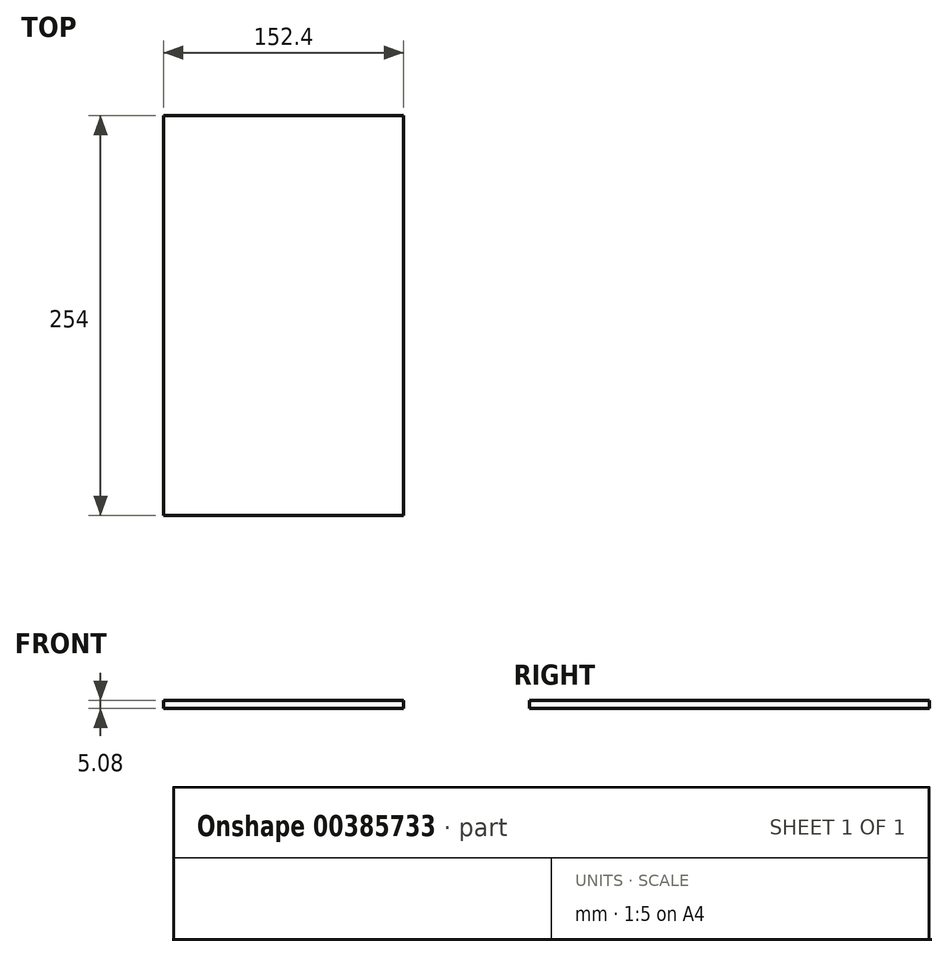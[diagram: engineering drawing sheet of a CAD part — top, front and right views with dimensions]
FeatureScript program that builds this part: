
annotation { "Feature Type Name" : "Feature", "Feature Type Description" : "" }
export const myFeature = defineFeature(function(context is Context, id is Id, definition is map)
    precondition{}
    {
        {
            var Q0;
            Q0=qCreatedBy(makeId("Front.planeOp"),FACE);
            var sketch = newSketch(context, id + "F0", { "sketchPlane" : qUnion([Q0])});
            skLineSegment(sketch, "E0.bottom", {"start": v(-76.2, 2.54) * mm, "end": v(76.2, 2.54) * mm});
            skLineSegment(sketch, "E0.top", {"start": v(-76.2, -2.54) * mm, "end": v(76.2, -2.54) * mm});
            skLineSegment(sketch, "E0.left", {"start": v(-76.2, 2.54) * mm, "end": v(-76.2, -2.54) * mm});
            skLineSegment(sketch, "E0.right", {"start": v(76.2, 2.54) * mm, "end": v(76.2, -2.54) * mm});
            skPoint(sketch, "E0.middle", {"position": v(0, 0) * mm});
            skSolve(sketch);
        }
        {
            var Q0;
            Q0=qSketchRegion(id+"F0",true);
            extrude(context, id + "F1", {"entities" : qUnion([Q0]), "depth" : 254 * mm});
        }
    });
